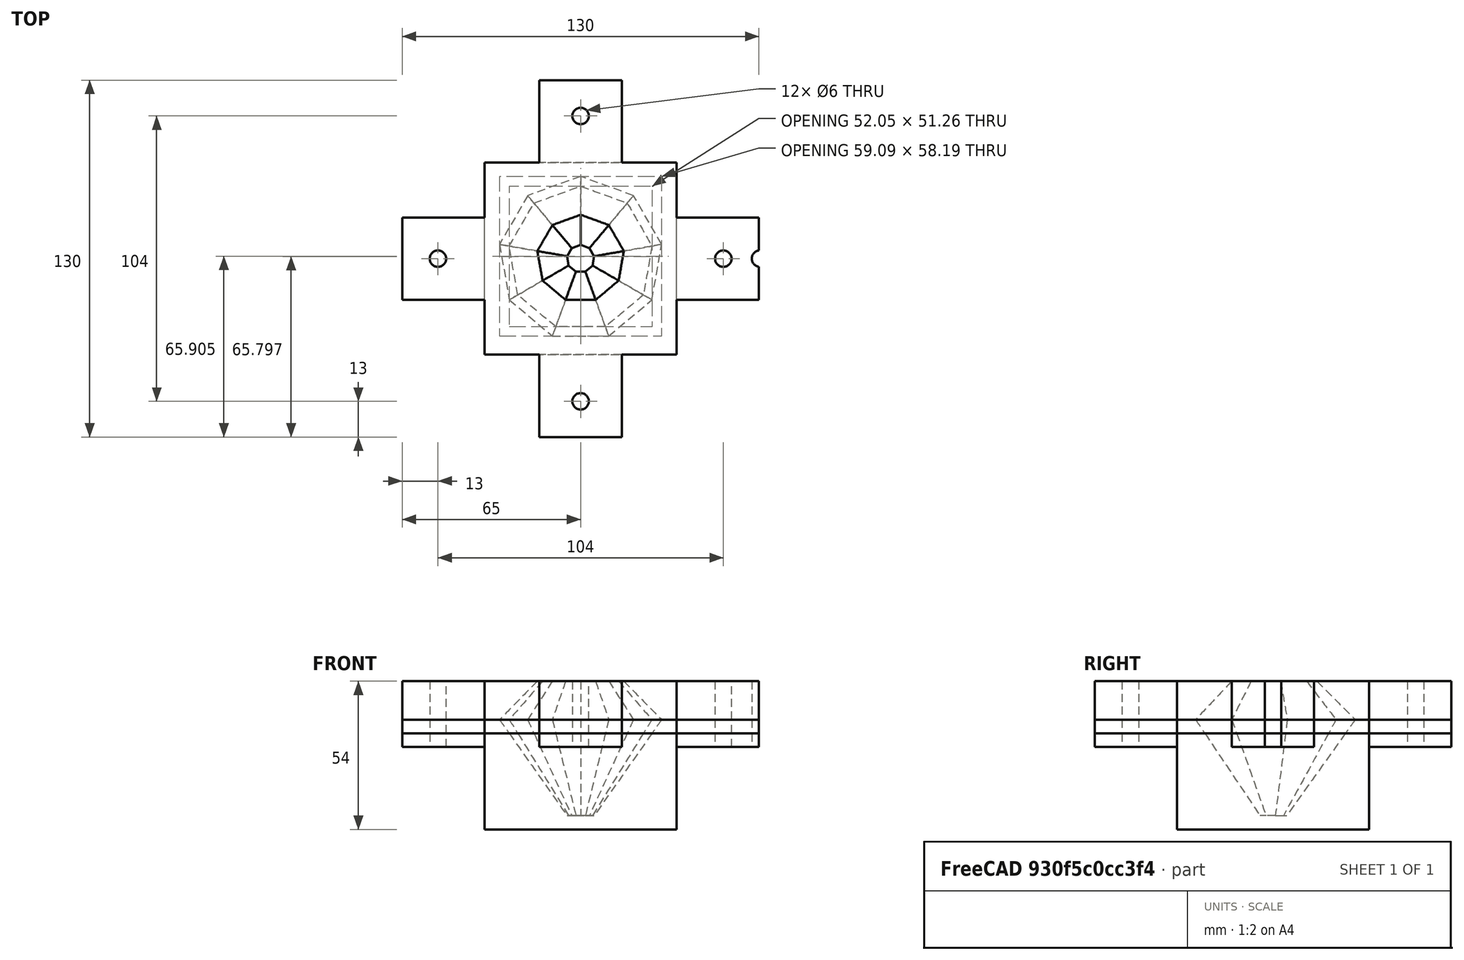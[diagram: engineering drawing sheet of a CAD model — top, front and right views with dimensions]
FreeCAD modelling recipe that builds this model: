
FCSTD DOCUMENT  (FreeCAD 0.20R29410 (Git))
Label: izumrud
License: All rights reserved
LicenseURL: http://en.wikipedia.org/wiki/All_rights_reserved
objects: Part::Cut×14, Part::Box×10, Part::Cylinder×5, Part::FeaturePython×5, Part::Plane×2, Part::Loft×1, Part::MultiFuse×1
note: 38 computed .brp shape members not serialized (recipe doc carries the construction recipe); baked Part::Feature solids carry a one-line shape summary decoded from their .brp

FEATURE [Part::Loft] Loft
  Closed = false
  MaxDegree = 5
  Ruled = true
  Solid = true
FEATURE [Part::Box] Box  label="Cube"
  AttacherType = Attacher::AttachEngine3D
  Height = 54
  Length = 70
  Placement = pos=(-35,-35,-40) rot=(0,0,1;0rad)
  Width = 70
FEATURE [Part::Box] Box001  label="Cube001"
  AttacherType = Attacher::AttachEngine3D
  Height = 24
  Length = 130
  Placement = pos=(-65,-65,-10) rot=(0,0,1;0rad)
  Width = 130
FEATURE [Part::Cylinder] Cylinder
  Angle = 360
  AttacherType = Attacher::AttachEngine3D
  FirstAngle = 0
  Height = 30
  Placement = pos=(52,0,-15) rot=(0,0,1;0rad)
  Radius = 3
  SecondAngle = 0
FEATURE [Part::Cylinder] Cylinder001
  Angle = 360
  AttacherType = Attacher::AttachEngine3D
  FirstAngle = 0
  Height = 30
  Placement = pos=(0,52,-15) rot=(0,0,1;0rad)
  Radius = 3
  SecondAngle = 0
FEATURE [Part::Cylinder] Cylinder002
  Angle = 360
  AttacherType = Attacher::AttachEngine3D
  FirstAngle = 0
  Height = 30
  Placement = pos=(0,-52,-15) rot=(0,0,1;0rad)
  Radius = 3
  SecondAngle = 0
FEATURE [Part::Cylinder] Cylinder003
  Angle = 360
  AttacherType = Attacher::AttachEngine3D
  FirstAngle = 0
  Height = 30
  Placement = pos=(-52,0,-15) rot=(0,0,1;0rad)
  Radius = 3
  SecondAngle = 0
FEATURE [Part::MultiFuse] Fusion
  Shapes = -> [Box001,Box]
FEATURE [Part::Cut] Cut
  Base = -> Fusion
  Tool = -> Loft
FEATURE [Part::Plane] Plane
  AttacherType = Attacher::AttachEngine3D
  Length = 170
  Placement = pos=(-81.9,-83.9,-5) rot=(0,0,1;0rad)
  Width = 170
FEATURE [Part::Plane] Plane001
  AttacherType = Attacher::AttachEngine3D
  Length = 170
  Placement = pos=(-81.9,-83.9,0) rot=(0,0,1;0rad)
  Width = 170
FEATURE [Part::Cut] Cut001
  Base = -> Cut
  Tool = -> Cylinder
FEATURE [Part::Cut] Cut002
  Base = -> Cut001
  Tool = -> Cylinder001
FEATURE [Part::Cut] Cut003
  Base = -> Cut002
  Tool = -> Cylinder003
FEATURE [Part::Cut] Cut004
  Base = -> Cut003
  Tool = -> Cylinder002
FEATURE [Part::Box] Box002  label="Cube002"
  AttacherType = Attacher::AttachEngine3D
  Height = 30
  Length = 30
  Placement = pos=(35,-65,-15) rot=(0,0,1;0rad)
  Width = 50
FEATURE [Part::Box] Box003  label="Cube003"
  AttacherType = Attacher::AttachEngine3D
  Height = 30
  Length = 30
  Placement = pos=(35,15,-15) rot=(0,0,1;0rad)
  Width = 50
FEATURE [Part::Box] Box004  label="Cube004"
  AttacherType = Attacher::AttachEngine3D
  Height = 30
  Length = 30
  Placement = pos=(-65,-65,-15) rot=(0,0,1;0rad)
  Width = 50
FEATURE [Part::Box] Box005  label="Cube005"
  AttacherType = Attacher::AttachEngine3D
  Height = 30
  Length = 30
  Placement = pos=(-65,15,-15) rot=(0,0,1;0rad)
  Width = 50
FEATURE [Part::Box] Box006  label="Cube006"
  AttacherType = Attacher::AttachEngine3D
  Height = 30
  Length = 50
  Placement = pos=(-65,35,-15) rot=(0,0,1;0rad)
  Width = 30
FEATURE [Part::Box] Box007  label="Cube007"
  AttacherType = Attacher::AttachEngine3D
  Height = 30
  Length = 50
  Placement = pos=(-65,-65,-15) rot=(0,0,1;0rad)
  Width = 30
FEATURE [Part::Box] Box008  label="Cube008"
  AttacherType = Attacher::AttachEngine3D
  Height = 30
  Length = 50
  Placement = pos=(15,-65,-15) rot=(0,0,1;0rad)
  Width = 30
FEATURE [Part::Box] Box009  label="Cube009"
  AttacherType = Attacher::AttachEngine3D
  Height = 30
  Length = 50
  Placement = pos=(15,35,-15) rot=(0,0,1;0rad)
  Width = 30
FEATURE [Part::Cut] Cut005
  Base = -> Cut004
  Tool = -> Box002
FEATURE [Part::Cut] Cut006
  Base = -> Cut005
  Tool = -> Box009
FEATURE [Part::Cut] Cut007
  Base = -> Cut006
  Tool = -> Box007
FEATURE [Part::Cut] Cut008
  Base = -> Cut007
  Tool = -> Box006
FEATURE [Part::Cut] Cut009
  Base = -> Cut008
  Tool = -> Box004
FEATURE [Part::Cut] Cut010
  Base = -> Cut009
  Tool = -> Box008
FEATURE [Part::Cut] Cut011
  Base = -> Cut010
  Tool = -> Box005
FEATURE [Part::Cut] Cut012
  Base = -> Cut011
  Tool = -> Box003
FEATURE [Part::Cylinder] Cylinder004
  Angle = 360
  AttacherType = Attacher::AttachEngine3D
  FirstAngle = 0
  Height = 30
  Placement = pos=(65.4,0,-15) rot=(0,0,1;0rad)
  Radius = 3
  SecondAngle = 0
FEATURE [Part::Cut] Cut013
  Base = -> Cut012
  Tool = -> Cylinder004
FEATURE [Part::FeaturePython] Slice  # WARN: FeaturePython — macro-defined, semantics opaque (R4)
  Base = -> Cut013
  Mode = 1
  Tolerance = 0
  Tools = -> [Plane001]
FEATURE [Part::FeaturePython] Slice_child0  label="top"  # WARN: FeaturePython — macro-defined, semantics opaque (R4)
  Base = -> Slice
  FilterType = 1
  Invert = false
  OverrideMaxVal = 0
  WindowFrom = 80
  WindowTo = 100
  items = 0
FEATURE [Part::FeaturePython] Slice001  # WARN: FeaturePython — macro-defined, semantics opaque (R4)
  Mode = 1
  Tolerance = 0
  Tools = -> [Plane]
FEATURE [Part::FeaturePython] Slice001_child0  label="mid"  # WARN: FeaturePython — macro-defined, semantics opaque (R4)
  Base = -> Slice001
  FilterType = 1
  Invert = false
  OverrideMaxVal = 0
  WindowFrom = 80
  WindowTo = 100
  items = 0
FEATURE [Part::FeaturePython] Slice001_child1  label="bottom"  # WARN: FeaturePython — macro-defined, semantics opaque (R4)
  Base = -> Slice001
  FilterType = 1
  Invert = false
  OverrideMaxVal = 0
  WindowFrom = 80
  WindowTo = 100
  items = 1
